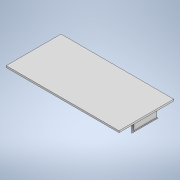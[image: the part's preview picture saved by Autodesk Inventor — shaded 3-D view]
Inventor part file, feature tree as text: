
AUTODESK INVENTOR PART (.ipt)
format: ipt  version: 2021 (Build 250183000, 183)  size: 149,504 bytes
history: native  units: mm
features: extrude x5, sketch x5, other x1
ambient origin geometry x8: Origin, YZ Plane, XZ Plane, XY Plane, X Axis, Y Axis, Z Axis, Center Point
bodies: Body1 (feature_tree)
feature tree (11):
  other  "Sólido1"
  extrude  "Extrusión1"  Depth=1.5mm TaperAngle=0.0deg
  extrude  "Extrusión2"  Depth=1.0mm TaperAngle=0.0deg
  extrude  "Extrusión3"  Depth=1.0mm TaperAngle=0.0deg
  extrude  "Extrusión4"  [1 undecoded]
  extrude  "Extrusión5"  [1 undecoded]
  sketch  "Boceto1"  dims[d0=1.5mm d1=0.0mm d2=10.0mm d3=0.0mm]
  sketch  "Boceto2"  dims[d4=3.0mm d5=1.0mm d6=0.0mm]
  sketch  "Boceto3"  dims[d8=3.0mm d9=1.0mm d10=0.0mm]
  sketch  "Boceto5"  dims[d11=48.25mm d12=0.0mm]
  sketch  "Boceto7"
note: 2 required parameter values undecoded (feature->parameter linkage not recoverable at this tier; creation-order binding heuristic only, values carry confidence <= 0.55)
